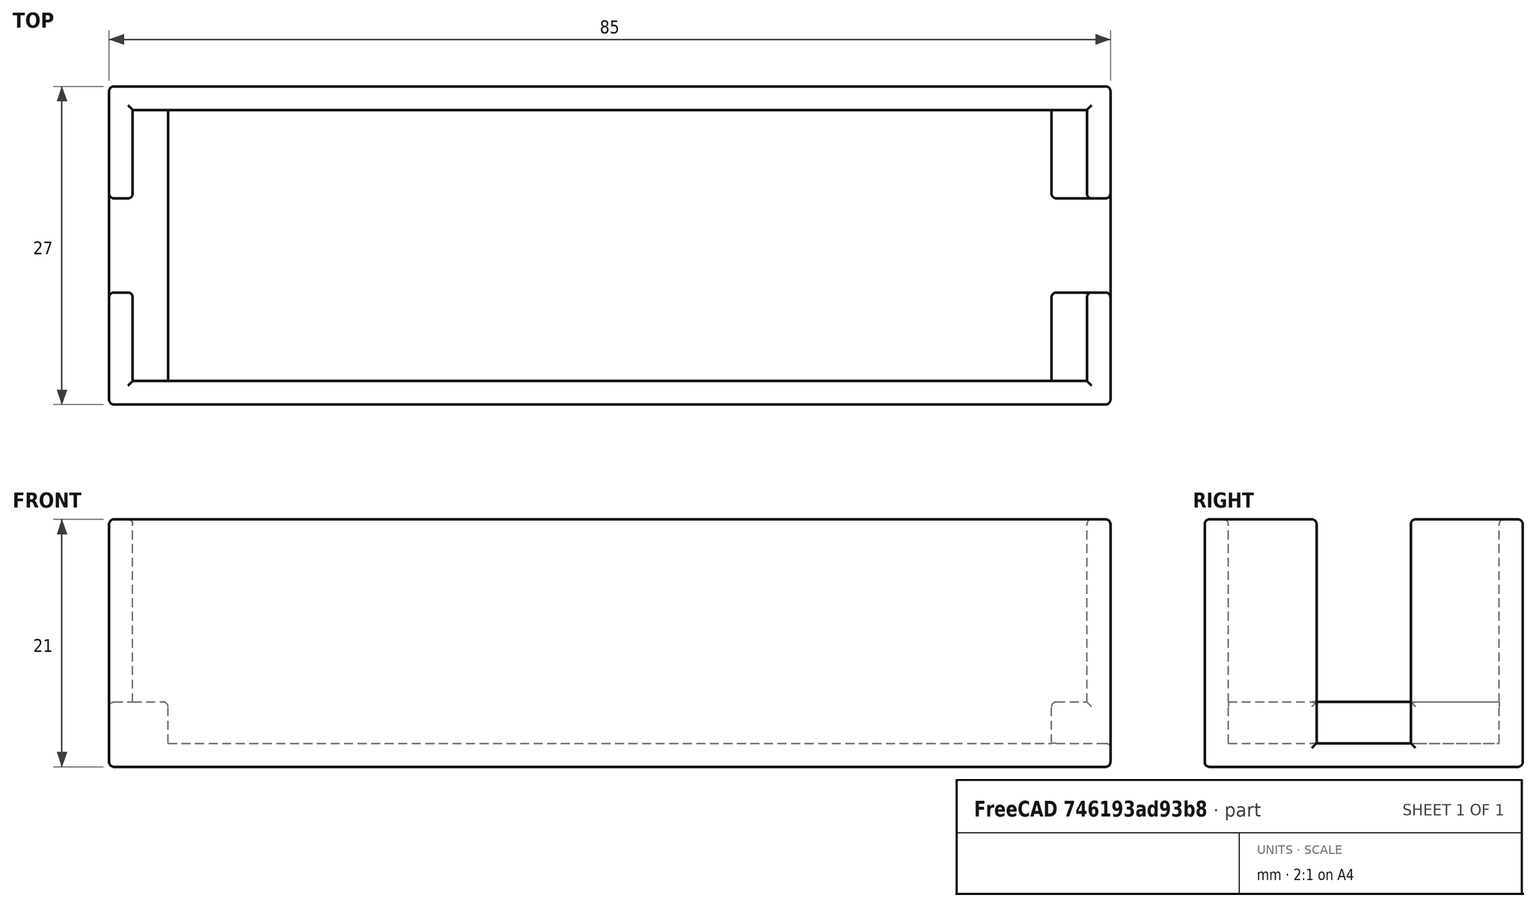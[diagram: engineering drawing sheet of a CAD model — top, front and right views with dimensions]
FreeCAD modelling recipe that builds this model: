
FCSTD DOCUMENT  (FreeCAD 0.18R16146 (Git))
Label: GehauseSwitch
License: All rights reserved
LicenseURL: http://en.wikipedia.org/wiki/All_rights_reserved
objects: Part::Box×5, Part::Cut×4, Part::Fillet×1
note: 10 computed .brp shape members not serialized (recipe doc carries the construction recipe); baked Part::Feature solids carry a one-line shape summary decoded from their .brp

FEATURE [Part::Box] Box  label="Cube"
  AttacherType = Attacher::AttachEngine3D
  Height = 21
  Length = 85
  Width = 27
FEATURE [Part::Box] Box001  label="Cube001"
  AttacherType = Attacher::AttachEngine3D
  Height = 30
  Length = 75
  Placement = pos=(5,2,2) rot=(0,0,1;0rad)
  Width = 23
FEATURE [Part::Box] Box002  label="Cube002"
  AttacherType = Attacher::AttachEngine3D
  Height = 30
  Length = 81
  Placement = pos=(2,2,5.5) rot=(0,0,1;0rad)
  Width = 23
FEATURE [Part::Cut] Cut
  Base = -> Box
  Tool = -> Box002
FEATURE [Part::Cut] Cut001
  Base = -> Cut
  Tool = -> Box001
FEATURE [Part::Box] Box003  label="Cube003"
  AttacherType = Attacher::AttachEngine3D
  Height = 30
  Length = 10
  Placement = pos=(-2,9.5,5.5) rot=(0,0,1;0rad)
  Width = 8
FEATURE [Part::Box] Box004  label="Cube004"
  AttacherType = Attacher::AttachEngine3D
  Height = 30
  Length = 10
  Placement = pos=(80,9.5,2) rot=(0,0,1;0rad)
  Width = 8
FEATURE [Part::Cut] Cut002
  Base = -> Cut001
  Tool = -> Box003
FEATURE [Part::Cut] Cut003
  Base = -> Cut002
  Tool = -> Box004
FEATURE [Part::Fillet] Fillet
  Base = -> Cut003
  Edges = 47 edges r=0.4: [Edge1,Edge2,Edge3,Edge4,Edge5,Edge6,Edge7,Edge8,Edge9,Edge10,Edge11,Edge12,Edge13,Edge14,Edge15,Edge16,Edge17,Edge18,Edge22,Edge23,Edge24,Edge25,Edge26,Edge27,Edge28,Edge29,Edge30,Edge31,Edge32,Edge33,Edge34,Edge35,Edge36,Edge45,Edge48,Edge49,Edge50,Edge51,Edge52,Edge54,Edge59,Edge60,Edge61,Edge69,+3 more]
